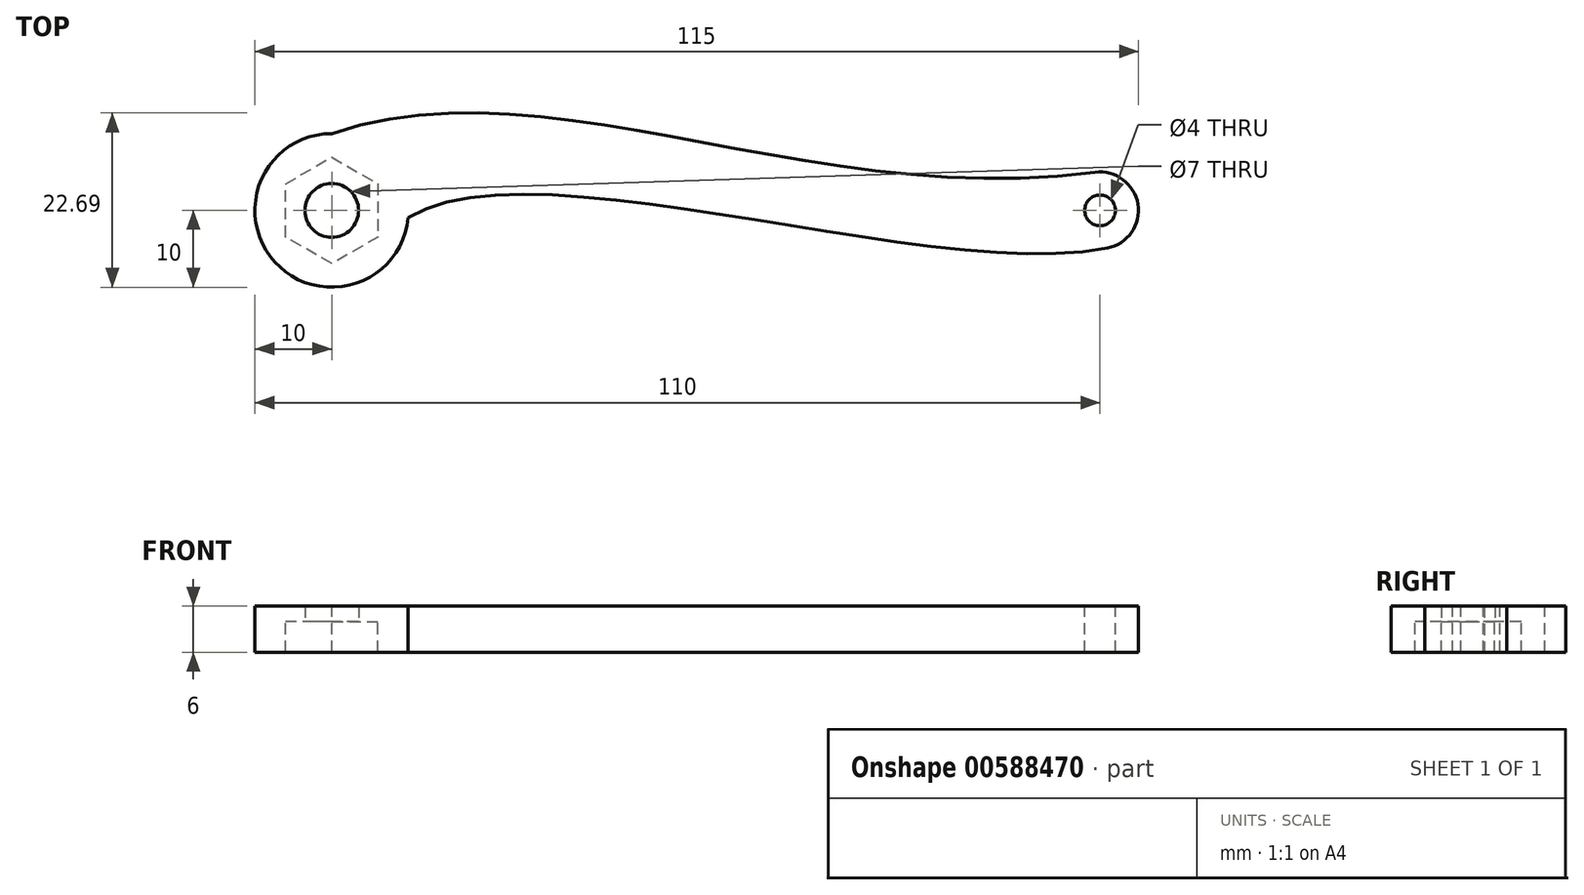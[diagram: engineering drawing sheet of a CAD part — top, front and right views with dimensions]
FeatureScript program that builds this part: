
annotation { "Feature Type Name" : "Feature", "Feature Type Description" : "" }
export const myFeature = defineFeature(function(context is Context, id is Id, definition is map)
    precondition{}
    {
        {
            var Q0;
            Q0=qCreatedBy(makeId("Top.planeOp"),FACE);
            var sketch = newSketch(context, id + "F0", { "sketchPlane" : qUnion([Q0])});
            skCircle(sketch, "E0.cCircle", {"center": v(0, 0) * mm, "radius": 6 * mm, "construction": true});
            skLineSegment(sketch, "E0.0", {"start": v(6, 3.46) * mm, "end": v(6, -3.46) * mm});
            skLineSegment(sketch, "E0.1", {"start": v(6, -3.46) * mm, "end": v(0, -6.93) * mm});
            skLineSegment(sketch, "E0.2", {"start": v(0, -6.93) * mm, "end": v(-6, -3.46) * mm});
            skLineSegment(sketch, "E0.3", {"start": v(-6, -3.46) * mm, "end": v(-6, 3.46) * mm});
            skLineSegment(sketch, "E0.4", {"start": v(-6, 3.46) * mm, "end": v(0, 6.93) * mm});
            skLineSegment(sketch, "E0.5", {"start": v(0, 6.93) * mm, "end": v(6, 3.46) * mm});
            skPoint(sketch, "E0.0.midPoint", {"position": v(6, 0) * mm});
            skCircle(sketch, "E1", {"center": v(0, 0) * mm, "radius": 10 * mm});
            skFitSpline(sketch, "E2", {"points": [v(0, 10) * mm, v(99.52, 4.98) * mm], "startDerivative": vector(84.88, 28.85) * mm, "endDerivative": vector(113.07, 14.94) * mm});
            skFitSpline(sketch, "E3", {"points": [v(9.95, -0.96) * mm, v(101.62, -4.77) * mm], "startDerivative": vector(49.36, 30.6) * mm, "endDerivative": vector(69.48, 15.22) * mm});
            skCircle(sketch, "E4", {"center": v(100, 0) * mm, "radius": 5 * mm});
            skCircle(sketch, "E5", {"center": v(100, 0) * mm, "radius": 2 * mm});
            skCircle(sketch, "E6", {"center": v(0, 0) * mm, "radius": 3.5 * mm});
            skSolve(sketch);
        }
        {
            var Q0;
            Q0 = qSketchRegion(id + "F0", true);
            extrude(context, id + "F1", {"entities" : qUnion([Q0]), "oppositeDirection" : true, "depth" : 4 * mm, "offsetDistance" : 25 * mm});
        }
        {
            var Q0;
            Q0 = qSketchRegion(id + "F0", true);
            var Q1;
            Q1=makeQuery(id+"F0.imprint","IMPRINT",FACE,{"disambiguationData":[TD([[makeQuery(id+"F0.imprint","IMPRINT",EDGE,{"derivedFrom":sQuery(id+"F0.wireOp",EDGE,"E0.0")}),-1.0]])]});
            extrude(context, id + "F2", {"entities" : qUnion([Q0, Q1]), "operationType" : NewBodyOperationType.ADD, "depth" : 2 * mm, "offsetDistance" : 25 * mm});
        }
    });
